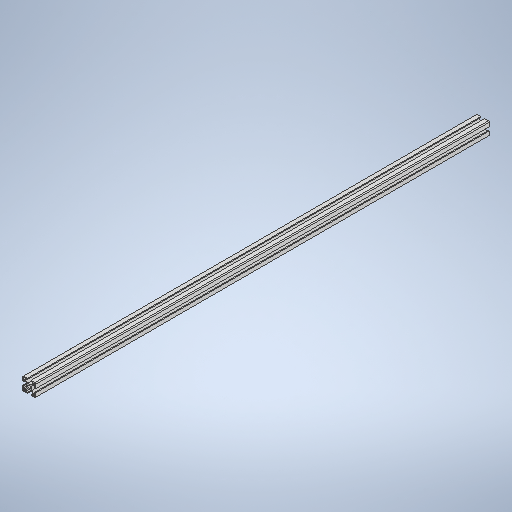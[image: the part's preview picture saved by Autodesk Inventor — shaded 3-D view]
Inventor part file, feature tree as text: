
AUTODESK INVENTOR PART (.ipt)
format: ipt  version: 2025 (Build 290162000, 162)  size: 310,784 bytes
history: native  units: in
note: dims shown in document units (in); Inventor stores cm internally (conversion verified against a paired STEP export)
features: extrude x1, sketch x1
ambient origin geometry x8: Origin, YZ Plane, XZ Plane, XY Plane, X Axis, Y Axis, Z Axis, Center Point
bodies: Solid1 (feature_tree)
feature tree (2):
  extrude  "Extrusion1"  Depth=40.9449in
  sketch  "Sketch1"  dims[d6=40.9449in d7=0.0in d8=0.1969in d9=0.0344in]
